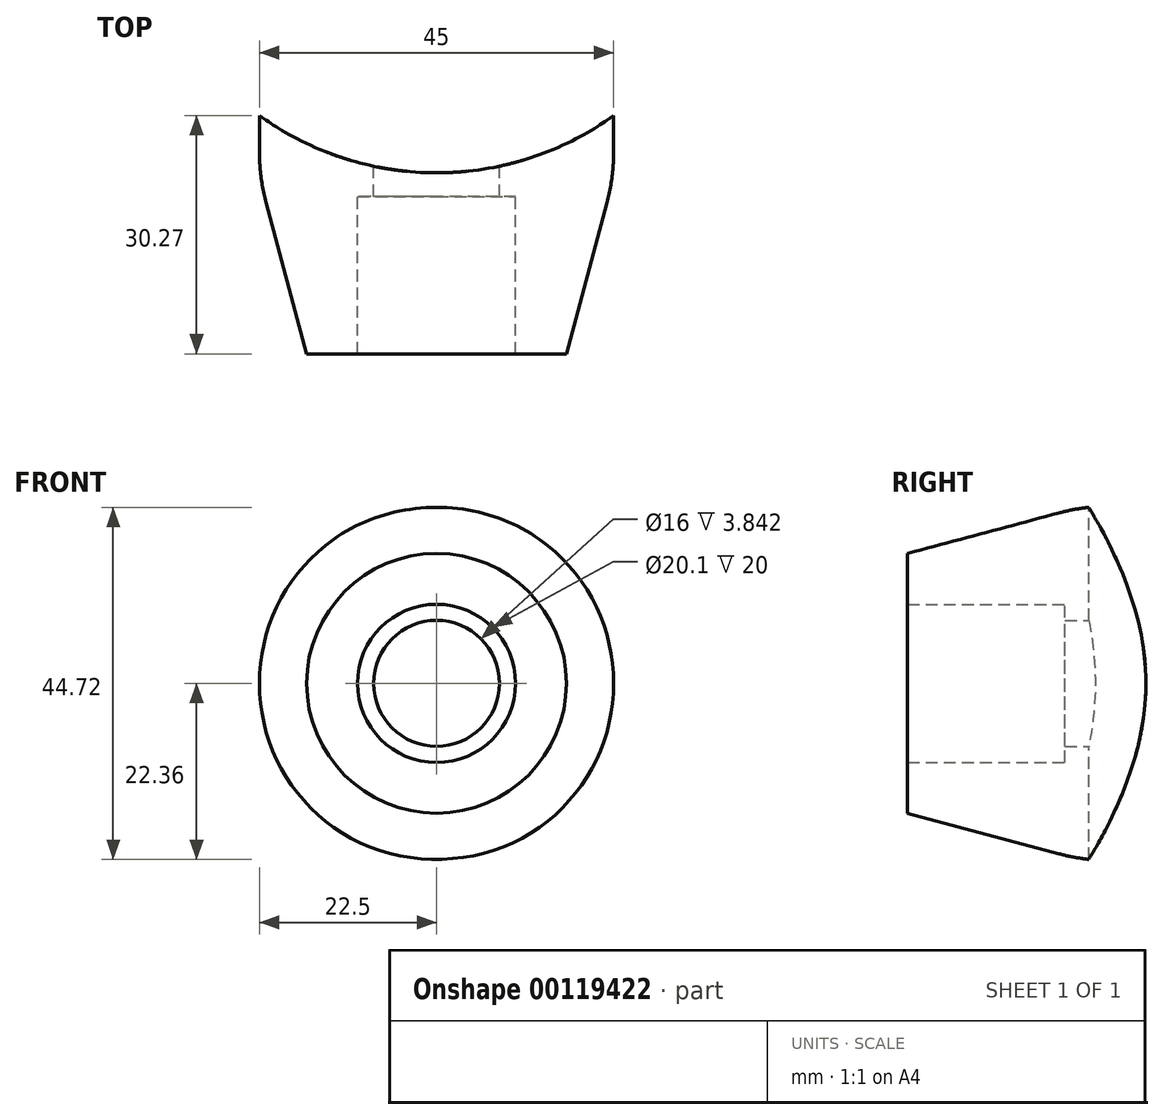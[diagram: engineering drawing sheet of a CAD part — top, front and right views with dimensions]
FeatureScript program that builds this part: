
annotation { "Feature Type Name" : "Feature", "Feature Type Description" : "" }
export const myFeature = defineFeature(function(context is Context, id is Id, definition is map)
    precondition{}
    {
        {
            var Q0;
            Q0=qCreatedBy(makeId("Top.planeOp"),FACE);
            var sketch = newSketch(context, id + "F0", { "sketchPlane" : qUnion([Q0])});
            skCircle(sketch, "E0", {"center": v(0, 0) * mm, "radius": 36.5 * mm});
            skCircle(sketch, "E1", {"center": v(0, 0) * mm, "radius": 38.45 * mm});
            skLineSegment(sketch, "E2", {"start": v(0, 0) * mm, "end": v(0, -38.45) * mm, "construction": true});
            skSolve(sketch);
        }
        {
            var Q0;
            Q0=qCreatedBy(makeId("Front.planeOp"),FACE);
            cPlane(context, id + "F1", {"entities" : qUnion([Q0]), "cplaneType" : CPlaneType.OFFSET, "offset" : 60 / 2 * mm, "width" : 150 * mm, "height" : 150 * mm});
        }
        {
            var Q0;
            Q0=qCreatedBy(id+"F1.planeOp",FACE);
            var sketch = newSketch(context, id + "F2", { "sketchPlane" : qUnion([Q0])});
            skCircle(sketch, "E3", {"center": v(0, 0) * mm, "radius": 15.85 * mm});
            skCircle(sketch, "E4", {"center": v(0, 0) * mm, "radius": 8 * mm});
            skCircle(sketch, "E5", {"center": v(0, 0) * mm, "radius": 22.5 * mm});
            skSolve(sketch);
        }
        {
            var Q0;
            Q0=makeQuery(id+"F2.imprint","IMPRINT",FACE,{"disambiguationData":[TD([[makeQuery(id+"F2.imprint","IMPRINT",EDGE,{"derivedFrom":sQuery(id+"F2.wireOp",EDGE,"E3")}),1.0]])]});
            extrude(context, id + "F3", {"entities" : qUnion([Q0]), "depth" : (76.9 / 2 - 30) * mm});
        }
        {
            var Q0;
            Q0=makeQuery(id+"F0.imprint","IMPRINT",FACE,{"disambiguationData":[TD([[makeQuery(id+"F0.imprint","IMPRINT",EDGE,{"derivedFrom":sQuery(id+"F0.wireOp",EDGE,"E0")}),1.0]])]});
            extrude(context, id + "F4", {"entities" : qUnion([Q0]), "operationType" : NewBodyOperationType.REMOVE, "endBound" : BoundingType.SYMMETRIC, "oppositeDirection" : true, "depth" : 39.33 * mm});
        }
        {
            var Q0;
            Q0=makeQuery(id+"F2.imprint","IMPRINT",FACE,{"disambiguationData":[TD([[makeQuery(id+"F2.imprint","IMPRINT",EDGE,{"derivedFrom":sQuery(id+"F2.wireOp",EDGE,"E3")}),-1.0]])]});
            extrude(context, id + "F5", {"entities" : qUnion([Q0]), "depth" : (76.9 / 2 - 30) * mm});
        }
        {
            var Q0;
            Q0=makeQuery(id+"F0.imprint","IMPRINT",FACE,{"disambiguationData":[TD([[makeQuery(id+"F0.imprint","IMPRINT",EDGE,{"derivedFrom":sQuery(id+"F0.wireOp",EDGE,"E0")}),-1.0]])]});
            var Q1;
            Q1=makeQuery(id+"F0.imprint","IMPRINT",FACE,{"disambiguationData":[TD([[makeQuery(id+"F0.imprint","IMPRINT",EDGE,{"derivedFrom":sQuery(id+"F0.wireOp",EDGE,"E0")}),1.0]])]});
            var Q2;
            Q2=sQuery(id+"F0.wireOp",EDGE,"E1");
            extrude(context, id + "F6", {"entities" : qUnion([Q0, Q1]), "operationType" : NewBodyOperationType.REMOVE, "surfaceEntities" : qUnion([Q2]), "endBound" : BoundingType.SYMMETRIC, "oppositeDirection" : true, "depth" : 59.97 * mm});
        }
        {
            var Q0;
            Q0=makeQuery(id+"F6.boolean.opBoolean","SPLIT",FACE,{"disambiguationData":[OD(0.0)],"derivedFrom":makeQuery(id+"F5.opExtrude","CAP_FACE",FACE,{"disambiguationData":[OSD([sQuery(id+"F2.wireOp",EDGE,"E3"),sQuery(id+"F2.wireOp",EDGE,"E5")])],"isStart":false})});
            var Q1;
            Q1=makeQuery(id+"F6.boolean.opBoolean","SPLIT",FACE,{"disambiguationData":[OD(1.0)],"derivedFrom":makeQuery(id+"F5.opExtrude","CAP_FACE",FACE,{"disambiguationData":[OSD([sQuery(id+"F2.wireOp",EDGE,"E3"),sQuery(id+"F2.wireOp",EDGE,"E5")])],"isStart":false})});
            var Q2;
            Q2=makeQuery(id+"F3.opExtrude","CAP_FACE",FACE,{"disambiguationData":[OSD([sQuery(id+"F2.wireOp",EDGE,"E3"),sQuery(id+"F2.wireOp",EDGE,"E4")])],"isStart":false});
            extrude(context, id + "F7", {"entities" : qUnion([Q0, Q1, Q2]), "operationType" : NewBodyOperationType.ADD, "depth" : 3 * mm});
        }
        {
            var Q0;
            {var subQ0=sQuery(id+"F2.wireOp",EDGE,"E5");var subQ1=sQuery(id+"F2.wireOp",EDGE,"E3");var subQ2=makeQuery(id+"F5.opExtrude","CAP_FACE",FACE,{"disambiguationData":[OSD([subQ1,subQ0])],"isStart":false});Q0=makeQuery(id+"F7.boolean.opBoolean","MERGE",FACE,{"derivedFrom":[makeQuery(id+"F7.opExtrude","CAP_FACE",FACE,{"disambiguationData":[OSD([subQ1,sQuery(id+"F2.wireOp",EDGE,"E4")])],"isStart":false}),makeQuery(id+"F7.opExtrude","CAP_FACE",FACE,{"disambiguationData":[OSD([subQ1,subQ0]),TDD([makeQuery(id+"F6.boolean.opBoolean","SPLIT",FACE,{"disambiguationData":[OD(0.0)],"derivedFrom":subQ2})])],"isStart":false}),makeQuery(id+"F7.opExtrude","CAP_FACE",FACE,{"disambiguationData":[OSD([subQ1,subQ0]),TDD([makeQuery(id+"F6.boolean.opBoolean","SPLIT",FACE,{"disambiguationData":[OD(1.0)],"derivedFrom":subQ2})])],"isStart":false})]});}
            var sketch = newSketch(context, id + "F8", { "sketchPlane" : qUnion([Q0])});
            skCircle(sketch, "E6", {"center": v(0, 0) * mm, "radius": 22.5 * mm});
            skCircle(sketch, "E7", {"center": v(0, 0) * mm, "radius": 8 * mm});
            skCircle(sketch, "E8", {"center": v(0, 0) * mm, "radius": 10.05 * mm});
            skSolve(sketch);
        }
        {
            var Q0;
            Q0=makeQuery(id+"F8.imprint","IMPRINT",FACE,{"disambiguationData":[TD([[makeQuery(id+"F8.imprint","IMPRINT",EDGE,{"derivedFrom":sQuery(id+"F8.wireOp",EDGE,"E6")}),1.0]])]});
            extrude(context, id + "F9", {"entities" : qUnion([Q0]), "operationType" : NewBodyOperationType.ADD, "depth" : 20 * mm});
        }
        {
            var Q0;
            Q0=makeQuery(id+"F9.opExtrude","CAP_EDGE",EDGE,{"disambiguationData":[OSD([sQuery(id+"F8.wireOp",EDGE,"E6")])],"isStart":false});
            chamfer(context, id + "F10", {"entities" : qUnion([Q0]), "chamferType" : ChamferType.OFFSET_ANGLE, "width" : 6 * mm, "oppositeDirection" : false, "angle" : 75 * degree, "tangentPropagation" : true});
        }
        {
            var Q0;
            {var subQ0=sQuery(id+"F8.wireOp",EDGE,"E6");var subQ1=sQuery(id+"F2.wireOp",EDGE,"E5");var subQ2=makeQuery(id+"F5.opExtrude","CAP_EDGE",EDGE,{"disambiguationData":[OSD([subQ1])],"isStart":false});var subQ3=makeQuery(id+"F5.opExtrude","SWEPT_FACE",FACE,{"disambiguationData":[OSD([subQ1])]});Q0=makeQuery(id+"F10.opChamfer","BLEND_EDGE",EDGE,{"blendedFrom":[makeQuery(id+"F9.opExtrude","CAP_EDGE",EDGE,{"disambiguationData":[OSD([subQ0])],"isStart":false}),makeQuery(id+"F9.boolean.opBoolean","MERGE",FACE,{"derivedFrom":[makeQuery(id+"F7.boolean.opBoolean","MERGE",FACE,{"derivedFrom":[makeQuery(id+"F6.boolean.opBoolean","SPLIT",FACE,{"disambiguationData":[OD(0.0)],"derivedFrom":subQ3}),makeQuery(id+"F6.boolean.opBoolean","SPLIT",FACE,{"disambiguationData":[OD(1.0)],"derivedFrom":subQ3}),makeQuery(id+"F7.opExtrude","SWEPT_FACE",FACE,{"disambiguationData":[OSD([subQ1]),TDD([makeQuery(id+"F6.boolean.opBoolean","SPLIT",EDGE,{"disambiguationData":[OD(0.0)],"derivedFrom":subQ2})])]}),makeQuery(id+"F7.opExtrude","SWEPT_FACE",FACE,{"disambiguationData":[OSD([subQ1]),TDD([makeQuery(id+"F6.boolean.opBoolean","SPLIT",EDGE,{"disambiguationData":[OD(1.0)],"derivedFrom":subQ2})])]})]}),makeQuery(id+"F9.opExtrude","SWEPT_FACE",FACE,{"disambiguationData":[OSD([subQ0])]})]})],"blendedInto":[makeQuery(id+"F9.boolean.opBoolean","MERGE",FACE,{"derivedFrom":[makeQuery(id+"F7.boolean.opBoolean","MERGE",FACE,{"derivedFrom":[makeQuery(id+"F6.boolean.opBoolean","SPLIT",FACE,{"disambiguationData":[OD(0.0)],"derivedFrom":subQ3}),makeQuery(id+"F6.boolean.opBoolean","SPLIT",FACE,{"disambiguationData":[OD(1.0)],"derivedFrom":subQ3}),makeQuery(id+"F7.opExtrude","SWEPT_FACE",FACE,{"disambiguationData":[OSD([subQ1]),TDD([makeQuery(id+"F6.boolean.opBoolean","SPLIT",EDGE,{"disambiguationData":[OD(0.0)],"derivedFrom":subQ2})])]}),makeQuery(id+"F7.opExtrude","SWEPT_FACE",FACE,{"disambiguationData":[OSD([subQ1]),TDD([makeQuery(id+"F6.boolean.opBoolean","SPLIT",EDGE,{"disambiguationData":[OD(1.0)],"derivedFrom":subQ2})])]})]}),makeQuery(id+"F9.opExtrude","SWEPT_FACE",FACE,{"disambiguationData":[OSD([subQ0])]})]})]});}
            fillet(context, id + "F11", {"entities" : qUnion([Q0]), "radius" : 25 * mm, "tangentPropagation" : true, "allowEdgeOverflow" : false});
        }
    });
